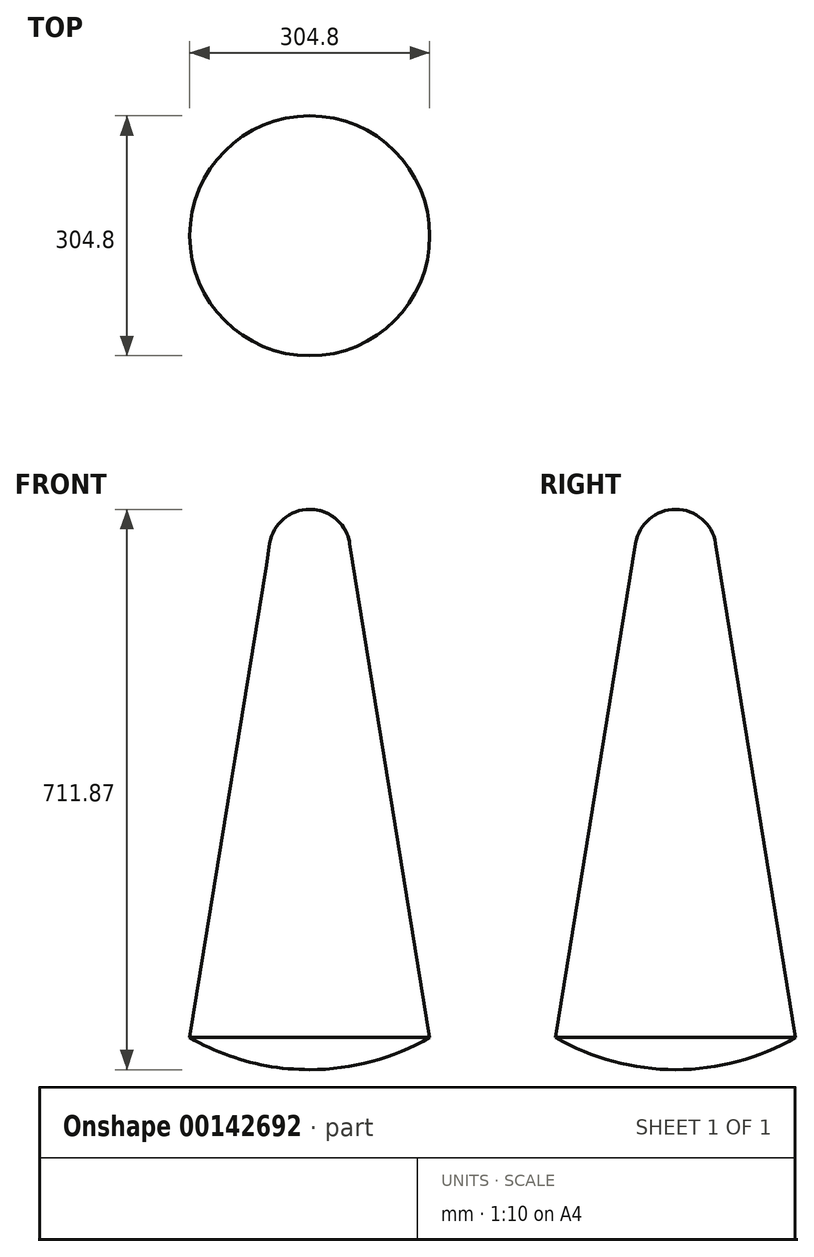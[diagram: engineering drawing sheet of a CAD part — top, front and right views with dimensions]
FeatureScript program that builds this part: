
annotation { "Feature Type Name" : "Feature", "Feature Type Description" : "" }
export const myFeature = defineFeature(function(context is Context, id is Id, definition is map)
    precondition{}
    {
        {
            var Q0;
            Q0=qCreatedBy(makeId("Front.planeOp"),FACE);
            var sketch = newSketch(context, id + "F0", { "sketchPlane" : qUnion([Q0])});
            skLineSegment(sketch, "E0", {"start": v(-304.8, 0) * mm, "end": v(-203.2, 627.79) * mm});
            skLineSegment(sketch, "E1", {"start": v(-101.6, 627.79) * mm, "end": v(0, 0) * mm});
            skArc(sketch, "E2", {"start": v(-304.8, 0) * mm, "mid": v(-152.4, -40.84) * mm, "end": v(0, 0) * mm});
            skArc(sketch, "E3", {"start": v(-101.6, 627.79) * mm, "mid": v(-152.4, 671.03) * mm, "end": v(-203.2, 627.79) * mm});
            skLineSegment(sketch, "E4", {"start": v(-203.2, 627.79) * mm, "end": v(-101.6, 627.79) * mm});
            skLineSegment(sketch, "E5", {"start": v(-152.4, 619.56) * mm, "end": v(-152.4, 263.96) * mm});
            skLineSegment(sketch, "E6", {"start": v(-152.4, 263.96) * mm, "end": v(-152.4, -186.34) * mm});
            skLineSegment(sketch, "E7", {"start": v(-152.4, -186.34) * mm, "end": v(-152.4, 619.56) * mm});
            skLineSegment(sketch, "E8", {"start": v(-152.4, 619.56) * mm, "end": v(-152.4, 775.94) * mm});
            skSolve(sketch);
        }
        {
            var Q0;
            {var subQ1=sQuery(id+"F0.wireOp",EDGE,"E3");var subQ3=sQuery(id+"F0.wireOp",EDGE,"E8");var subQ4=makeQuery(id+"F0.imprint","INTERSECT",VERTEX,{"derivedFrom":[subQ1,subQ3]});Q0=makeQuery(id+"F0.imprint","IMPRINT",FACE,{"disambiguationData":[TD([[makeQuery(id+"F0.imprint","IMPRINT",EDGE,{"disambiguationData":[TD([[subQ4,1.0]])],"derivedFrom":subQ3}),-1.0]])]});}
            var Q1;
            {var subQ4=sQuery(id+"F0.wireOp",EDGE,"E1");Q1=makeQuery(id+"F0.imprint","IMPRINT",FACE,{"disambiguationData":[TD([[makeQuery(id+"F0.imprint","IMPRINT",EDGE,{"derivedFrom":subQ4}),-1.0]])]});}
            var Q2;
            Q2=sQuery(id+"F0.wireOp",EDGE,"E8");
            revolve(context, id + "F1", {"entities" : qUnion([Q0, Q1]), "axis" : qUnion([Q2]), "revolveType" : RevolveType.FULL});
        }
    });
